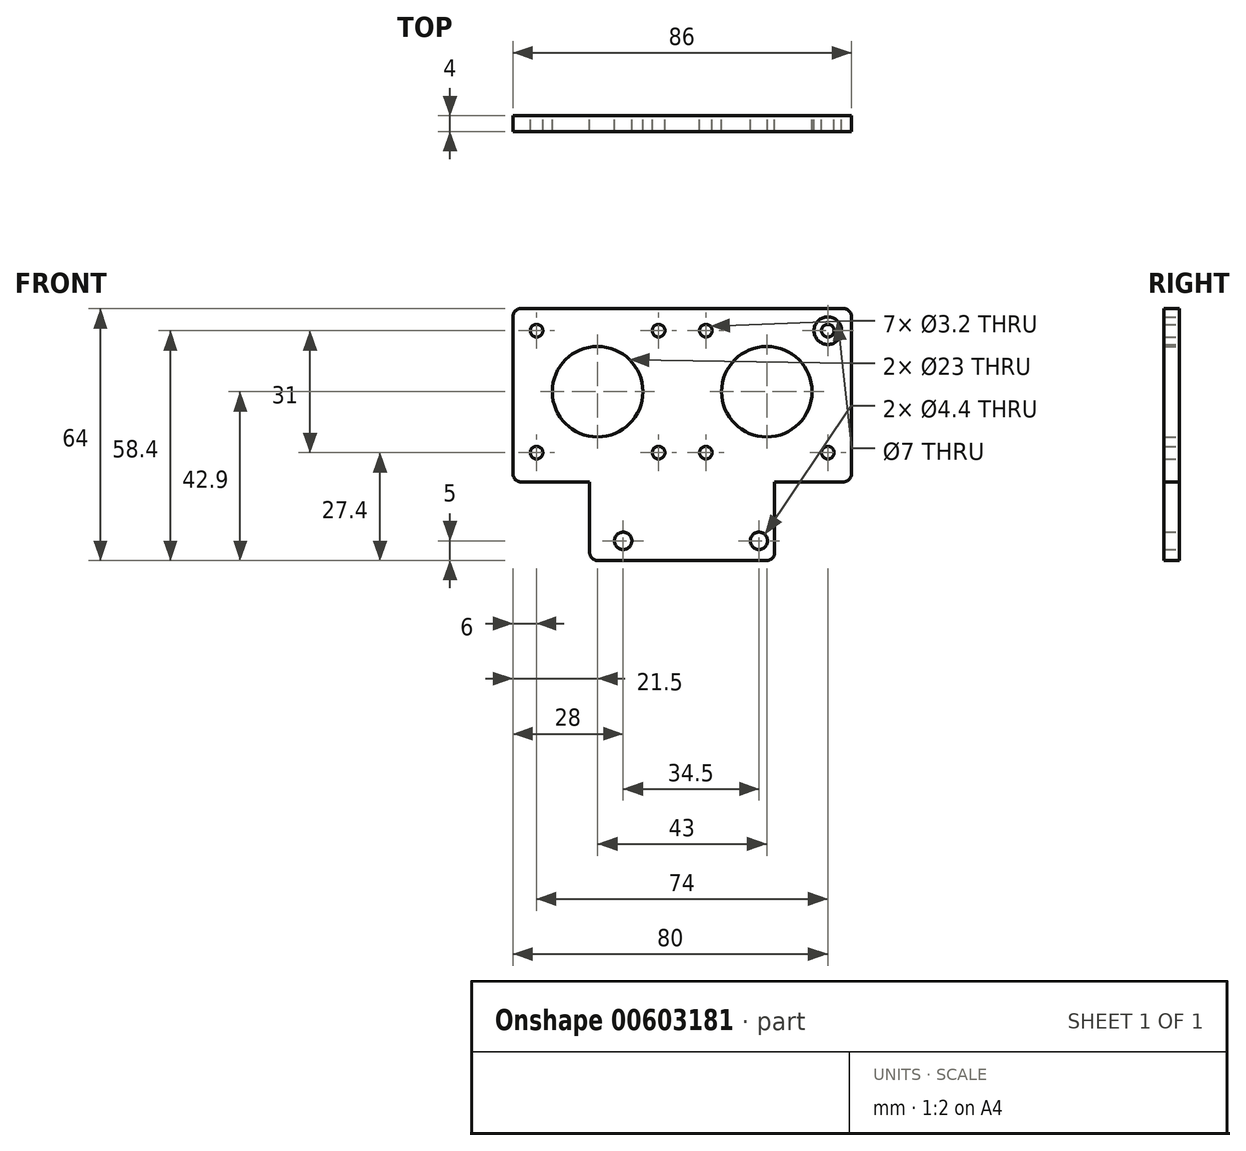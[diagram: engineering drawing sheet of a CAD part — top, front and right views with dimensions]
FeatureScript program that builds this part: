
annotation { "Feature Type Name" : "Feature", "Feature Type Description" : "" }
export const myFeature = defineFeature(function(context is Context, id is Id, definition is map)
    precondition{}
    {
        {
            var Q0;
            Q0=qCreatedBy(makeId("Front.planeOp"),FACE);
            var sketch = newSketch(context, id + "F0", { "sketchPlane" : qUnion([Q0])});
            skLineSegment(sketch, "E0.0", {"start": v(43, 89) * mm, "end": v(43, 45) * mm});
            skLineSegment(sketch, "E0.1", {"start": v(23.5, 25) * mm, "end": v(-23.5, 25) * mm});
            skLineSegment(sketch, "E0.2", {"start": v(-23.5, 25) * mm, "end": v(-23.5, 45) * mm});
            skCircle(sketch, "E0.3", {"center": v(-15, 30) * mm, "radius": 2.2 * mm});
            skCircle(sketch, "E0.4", {"center": v(19.5, 30) * mm, "radius": 2.2 * mm});
            skCircle(sketch, "E0.5", {"center": v(-6, 52.4) * mm, "radius": 1.6 * mm});
            skLineSegment(sketch, "E0.11", {"start": v(-43, 89) * mm, "end": v(43, 89) * mm});
            skLineSegment(sketch, "E0.12", {"start": v(-23.5, 45) * mm, "end": v(-43, 45) * mm});
            skLineSegment(sketch, "E0.15", {"start": v(-43, 45) * mm, "end": v(-43, 89) * mm});
            skCircle(sketch, "E0.16", {"center": v(-21.5, 67.9) * mm, "radius": 11.5 * mm});
            skLineSegment(sketch, "E1", {"start": v(43, 45) * mm, "end": v(23.5, 45) * mm});
            skLineSegment(sketch, "E2", {"start": v(23.5, 45) * mm, "end": v(23.5, 25) * mm});
            skCircle(sketch, "E3.1.0", {"center": v(-6, 83.4) * mm, "radius": 1.6 * mm});
            skCircle(sketch, "E3.2.0", {"center": v(-37, 83.4) * mm, "radius": 1.6 * mm});
            skCircle(sketch, "E3.3.0", {"center": v(-37, 52.4) * mm, "radius": 1.6 * mm});
            skCircle(sketch, "E4.0", {"center": v(-37, 83.4) * mm, "radius": 3.5 * mm});
            skLineSegment(sketch, "E5", {"start": v(0, 130.68) * mm, "end": v(0, 0) * mm, "construction": true});
            skCircle(sketch, "E6.MirrorC", {"center": v(37, 83.4) * mm, "radius": 1.6 * mm});
            skCircle(sketch, "E7.MirrorC", {"center": v(37, 83.4) * mm, "radius": 3.5 * mm});
            skCircle(sketch, "E8.MirrorC", {"center": v(37, 52.4) * mm, "radius": 1.6 * mm});
            skCircle(sketch, "E9.MirrorC", {"center": v(21.5, 67.9) * mm, "radius": 11.5 * mm});
            skCircle(sketch, "E10.MirrorC", {"center": v(6, 52.4) * mm, "radius": 1.6 * mm});
            skCircle(sketch, "E11.MirrorC", {"center": v(6, 83.4) * mm, "radius": 1.6 * mm});
            skSolve(sketch);
        }
        {
            var Q0;
            Q0=makeQuery(id+"F0.imprint","IMPRINT",FACE,{"disambiguationData":[TD([[makeQuery(id+"F0.imprint","IMPRINT",EDGE,{"derivedFrom":sQuery(id+"F0.wireOp",EDGE,"E0.0")}),-1.0]])]});
            var Q1;
            Q1=makeQuery(id+"F0.imprint","IMPRINT",FACE,{"disambiguationData":[TD([[makeQuery(id+"F0.imprint","IMPRINT",EDGE,{"derivedFrom":sQuery(id+"F0.wireOp",EDGE,"E3.2.0")}),-1.0]])]});
            var Q2;
            Q2=makeQuery(id+"F0.imprint","IMPRINT",FACE,{"disambiguationData":[TD([[makeQuery(id+"F0.imprint","IMPRINT",EDGE,{"derivedFrom":sQuery(id+"F0.wireOp",EDGE,"E6.MirrorC")}),1.0]])]});
            extrude(context, id + "F1", {"entities" : qUnion([Q0, Q1, Q2]), "depth" : 4 * mm, "offsetDistance" : 25 * mm});
        }
        {
            var Q0;
            Q0=makeQuery(id+"F1.opExtrude","SWEPT_EDGE",EDGE,{"disambiguationData":[OSD([sQuery(id+"F0.wireOp",EDGE,"E0.0"),sQuery(id+"F0.wireOp",EDGE,"E0.11")])]});
            var Q1;
            Q1=makeQuery(id+"F1.opExtrude","SWEPT_EDGE",EDGE,{"disambiguationData":[OSD([sQuery(id+"F0.wireOp",EDGE,"E0.0"),sQuery(id+"F0.wireOp",EDGE,"E1")])]});
            var Q2;
            Q2=makeQuery(id+"F1.opExtrude","SWEPT_EDGE",EDGE,{"disambiguationData":[OSD([sQuery(id+"F0.wireOp",EDGE,"E0.1"),sQuery(id+"F0.wireOp",EDGE,"E2")])]});
            var Q3;
            Q3=makeQuery(id+"F1.opExtrude","SWEPT_EDGE",EDGE,{"disambiguationData":[OSD([sQuery(id+"F0.wireOp",EDGE,"E0.11"),sQuery(id+"F0.wireOp",EDGE,"E0.15")])]});
            var Q4;
            Q4=makeQuery(id+"F1.opExtrude","SWEPT_EDGE",EDGE,{"disambiguationData":[OSD([sQuery(id+"F0.wireOp",EDGE,"E0.12"),sQuery(id+"F0.wireOp",EDGE,"E0.15")])]});
            var Q5;
            Q5=makeQuery(id+"F1.opExtrude","SWEPT_EDGE",EDGE,{"disambiguationData":[OSD([sQuery(id+"F0.wireOp",EDGE,"E0.1"),sQuery(id+"F0.wireOp",EDGE,"E0.2")])]});
            fillet(context, id + "F2", {"entities" : qUnion([Q0, Q1, Q2, Q3, Q4, Q5]), "radius" : 2 * mm, "tangentPropagation" : true, "allowEdgeOverflow" : false});
        }
    });
